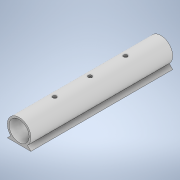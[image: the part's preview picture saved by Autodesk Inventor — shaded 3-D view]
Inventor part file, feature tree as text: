
AUTODESK INVENTOR PART (.ipt)
format: ipt  version: 2022 (Build 260153000, 153)  size: 166,912 bytes
history: native  units: in
note: dims shown in document units (in); Inventor stores cm internally (conversion verified against a paired STEP export)
features: extrude x7, sketch x7
ambient origin geometry x8: Origin, YZ Plane, XZ Plane, XY Plane, X Axis, Y Axis, Z Axis, Center Point
bodies: Solid1 (feature_tree)
feature tree (14):
  extrude  "Extrusion1"  Depth=4.7244in
  extrude  "Extrusion2"  Depth=2.3622in
  extrude  "Extrusion3"  Depth=2.3622in
  extrude  "Extrusion4"  Depth=0.126in
  extrude  "Extrusion6"  Depth=1.4001in TaperAngle=0.0deg
  extrude  "Extrusion7"  Depth=8.7874in TaperAngle=0.0deg
  extrude  "Extrusion8"  Depth=10.5251in TaperAngle=0.0deg
  sketch  "Sketch1"  dims[d0=0.7874in d1=4.7244in]
  sketch  "Sketch2"  dims[d2=0.7874in d3=0.0in d4=2.3622in]
  sketch  "Sketch3"  dims[d5=1.1811in d6=2.3622in]
  sketch  "Sketch4"  dims[d7=0.126in d8=0.126in]
  sketch  "Sketch6"  dims[d9=0.126in d10=1.4001in d11=0.0in]
  sketch  "Sketch7"  dims[d12=0.0787in d13=8.7874in d14=0.0in]
  sketch  "Sketch8"  dims[d15=0.6693in d16=10.5251in d17=0.0in d20=0.1181in d21=0.0in d22=4.7244in d23=0.0in d24=0.6693in d25=9.5256in d26=0.0in]
